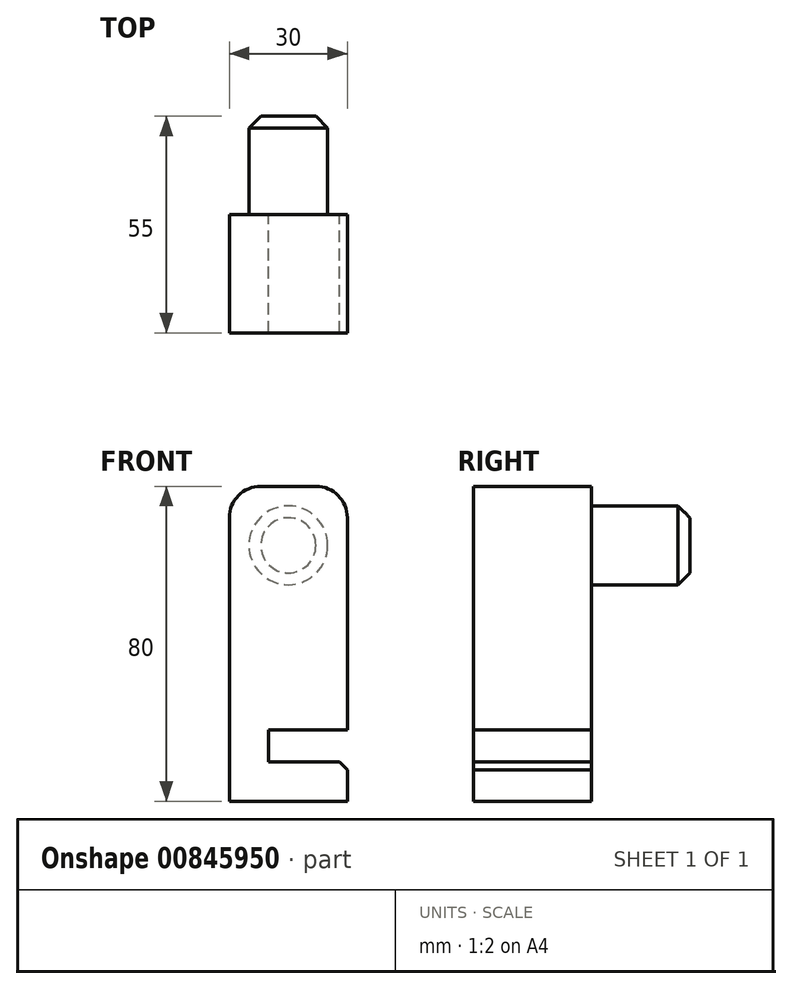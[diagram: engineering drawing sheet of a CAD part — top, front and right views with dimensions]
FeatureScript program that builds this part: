
annotation { "Feature Type Name" : "Feature", "Feature Type Description" : "" }
export const myFeature = defineFeature(function(context is Context, id is Id, definition is map)
    precondition{}
    {
        {
            var Q0;
            Q0=qCreatedBy(makeId("Top.planeOp"),FACE);
            var sketch = newSketch(context, id + "F0", { "sketchPlane" : qUnion([Q0])});
            skLineSegment(sketch, "E0.bottom", {"start": v(15, -15) * mm, "end": v(-15, -15) * mm});
            skLineSegment(sketch, "E0.top", {"start": v(15, 15) * mm, "end": v(-15, 15) * mm});
            skLineSegment(sketch, "E0.left", {"start": v(15, -15) * mm, "end": v(15, 15) * mm});
            skLineSegment(sketch, "E0.right", {"start": v(-15, -15) * mm, "end": v(-15, 15) * mm});
            skPoint(sketch, "E0.middle", {"position": v(0, 0) * mm});
            skSolve(sketch);
        }
        {
            var Q0;
            Q0=makeQuery(id+"F0.imprint","IMPRINT",FACE,{"disambiguationData":[TD([[makeQuery(id+"F0.imprint","IMPRINT",EDGE,{"derivedFrom":sQuery(id+"F0.wireOp",EDGE,"E0.bottom")}),-1.0]])]});
            extrude(context, id + "F1", {"entities" : qUnion([Q0]), "depth" : 80 * mm, "offsetDistance" : 25 * mm});
        }
        {
            var Q0;
            Q0=makeQuery(id+"F1.opExtrude","SWEPT_FACE",FACE,{"disambiguationData":[OSD([sQuery(id+"F0.wireOp",EDGE,"E0.left")])]});
            var sketch = newSketch(context, id + "F2", { "sketchPlane" : qUnion([Q0])});
            skLineSegment(sketch, "E1.bottom", {"start": v(-15, 10) * mm, "end": v(15, 10) * mm});
            skLineSegment(sketch, "E1.top", {"start": v(-15, 18.1) * mm, "end": v(15, 18.1) * mm});
            skLineSegment(sketch, "E1.left", {"start": v(-15, 10) * mm, "end": v(-15, 18.1) * mm});
            skLineSegment(sketch, "E1.right", {"start": v(15, 10) * mm, "end": v(15, 18.1) * mm});
            skSolve(sketch);
        }
        {
            var Q0;
            Q0 = qSketchRegion(id + "F2", true);
            extrude(context, id + "F3", {"entities" : qUnion([Q0]), "operationType" : NewBodyOperationType.REMOVE, "oppositeDirection" : true, "depth" : 20 * mm, "offsetDistance" : 25 * mm});
        }
        {
            var Q0;
            Q0=makeQuery(id+"F1.opExtrude","CAP_EDGE",EDGE,{"disambiguationData":[OSD([sQuery(id+"F0.wireOp",EDGE,"E0.left")])],"isStart":false});
            var Q1;
            Q1=makeQuery(id+"F1.opExtrude","CAP_EDGE",EDGE,{"disambiguationData":[OSD([sQuery(id+"F0.wireOp",EDGE,"E0.right")])],"isStart":false});
            fillet(context, id + "F4", {"entities" : qUnion([Q0, Q1]), "radius" : 8 * mm, "tangentPropagation" : true, "allowEdgeOverflow" : false});
        }
        {
            var Q0;
            Q0=makeQuery(id+"F3.boolean.opBoolean","COPY",EDGE,{"derivedFrom":makeQuery(id+"F3.opExtrude","CAP_EDGE",EDGE,{"disambiguationData":[OSD([sQuery(id+"F2.wireOp",EDGE,"E1.top")])],"isStart":true})});
            var Q1;
            Q1=makeQuery(id+"F3.boolean.opBoolean","COPY",EDGE,{"derivedFrom":makeQuery(id+"F3.opExtrude","CAP_EDGE",EDGE,{"disambiguationData":[OSD([sQuery(id+"F2.wireOp",EDGE,"E1.bottom")])],"isStart":true})});
            chamfer(context, id + "F5", {"entities" : qUnion([Q0, Q1]), "width" : 2 * mm, "tangentPropagation" : true});
        }
        {
            var Q0;
            Q0=makeQuery(id+"F1.opExtrude","SWEPT_FACE",FACE,{"disambiguationData":[OSD([sQuery(id+"F0.wireOp",EDGE,"E0.top")])]});
            var sketch = newSketch(context, id + "F6", { "sketchPlane" : qUnion([Q0])});
            skCircle(sketch, "E2", {"center": v(0, 65) * mm, "radius": 10 * mm});
            skSolve(sketch);
        }
        {
            var Q0;
            Q0 = qSketchRegion(id + "F6", true);
            extrude(context, id + "F7", {"entities" : qUnion([Q0]), "operationType" : NewBodyOperationType.ADD, "depth" : 25 * mm, "offsetDistance" : 25 * mm});
        }
        {
            var Q0;
            Q0=makeQuery(id+"F7.opExtrude","CAP_EDGE",EDGE,{"disambiguationData":[OSD([sQuery(id+"F6.wireOp",EDGE,"E2")])],"isStart":false});
            chamfer(context, id + "F8", {"entities" : qUnion([Q0]), "width" : 3 * mm, "tangentPropagation" : true});
        }
    });
